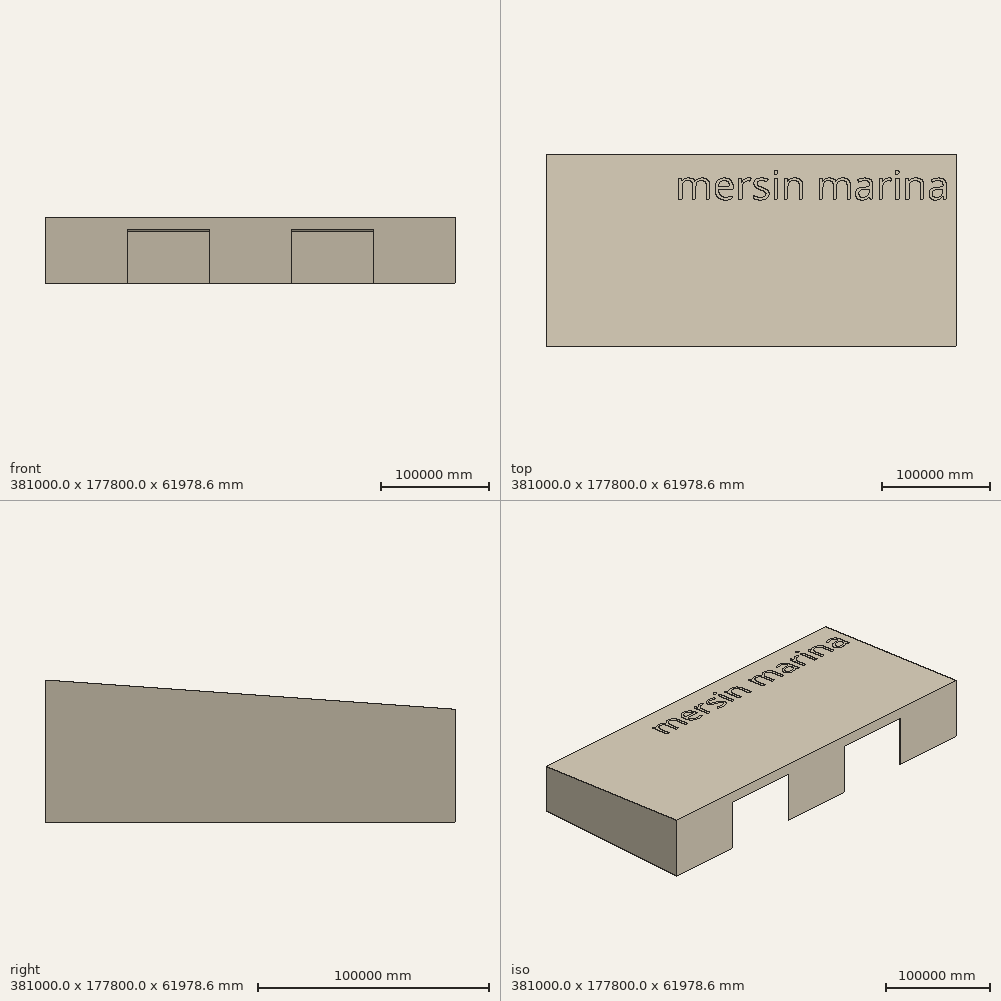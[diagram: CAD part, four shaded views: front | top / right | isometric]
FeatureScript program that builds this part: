
annotation { "Feature Type Name" : "Feature", "Feature Type Description" : "" }
export const myFeature = defineFeature(function(context is Context, id is Id, definition is map)
    precondition{}
    {
        {
            var Q0;
            Q0=qCreatedBy(makeId("Top.planeOp"),FACE);
            var sketch = newSketch(context, id + "F0", { "sketchPlane" : qUnion([Q0])});
            skLineSegment(sketch, "E0.bottom", {"start": v(0, 0) * mm, "end": v(381000, 0) * mm});
            skLineSegment(sketch, "E0.top", {"start": v(0, 177800) * mm, "end": v(381000, 177800) * mm});
            skLineSegment(sketch, "E0.left", {"start": v(0, 0) * mm, "end": v(0, 177800) * mm});
            skLineSegment(sketch, "E0.right", {"start": v(381000, 0) * mm, "end": v(381000, 177800) * mm});
            skLineSegment(sketch, "E1.0", {"start": v(1016, 176784) * mm, "end": v(379984, 176784) * mm});
            skLineSegment(sketch, "E1.1", {"start": v(1016, 1016) * mm, "end": v(1016, 176784) * mm});
            skLineSegment(sketch, "E1.2", {"start": v(1016, 1016) * mm, "end": v(379984, 1016) * mm});
            skLineSegment(sketch, "E1.3", {"start": v(379984, 1016) * mm, "end": v(379984, 176784) * mm});
            skSolve(sketch);
        }
        {
            var Q0;
            Q0 = qSketchRegion(id + "F0", true);
            extrude(context, id + "F1", {"entities" : qUnion([Q0]), "depth" : 60960 * mm, "offsetDistance" : 25.4 * mm});
        }
        {
            var Q0;
            Q0=makeQuery(id+"F1.opExtrude","SWEPT_FACE",FACE,{"disambiguationData":[OSD([sQuery(id+"F0.wireOp",EDGE,"E0.right")])]});
            var sketch = newSketch(context, id + "F2", { "sketchPlane" : qUnion([Q0])});
            skLineSegment(sketch, "E2", {"start": v(0, 60960) * mm, "end": v(177800, 48260) * mm});
            skLineSegment(sketch, "E3", {"start": v(177800, 48260) * mm, "end": v(177800, 60960) * mm});
            skLineSegment(sketch, "E4", {"start": v(177800, 60960) * mm, "end": v(0, 60960) * mm});
            skSolve(sketch);
        }
        {
            var Q0;
            Q0 = qSketchRegion(id + "F2", true);
            extrude(context, id + "F3", {"entities" : qUnion([Q0]), "operationType" : NewBodyOperationType.REMOVE, "oppositeDirection" : true, "depth" : 421894 * mm, "offsetDistance" : 25.4 * mm});
        }
        {
            var Q0;
            Q0=makeQuery(id+"F1.opExtrude","SWEPT_FACE",FACE,{"disambiguationData":[OSD([sQuery(id+"F0.wireOp",EDGE,"E0.right")])]});
            var sketch = newSketch(context, id + "F4", { "sketchPlane" : qUnion([Q0])});
            skLineSegment(sketch, "E5", {"start": v(177800, 48260) * mm, "end": v(0, 60960) * mm});
            skLineSegment(sketch, "E6.0", {"start": v(177800, 49278.59) * mm, "end": v(0, 61978.59) * mm});
            skLineSegment(sketch, "E7", {"start": v(0, 61978.59) * mm, "end": v(0, 60960) * mm});
            skLineSegment(sketch, "E8", {"start": v(177800, 48260) * mm, "end": v(177800, 49278.59) * mm});
            skSolve(sketch);
        }
        {
            var Q0;
            Q0 = qSketchRegion(id + "F4", true);
            extrude(context, id + "F5", {"entities" : qUnion([Q0]), "operationType" : NewBodyOperationType.ADD, "oppositeDirection" : true, "depth" : 381000 * mm, "offsetDistance" : 25.4 * mm});
        }
        {
            var Q0;
            Q0=makeQuery(id+"F1.opExtrude","SWEPT_FACE",FACE,{"disambiguationData":[OSD([sQuery(id+"F0.wireOp",EDGE,"E0.bottom")])]});
            var sketch = newSketch(context, id + "F6", { "sketchPlane" : qUnion([Q0])});
            skLineSegment(sketch, "E9.bottom", {"start": v(76200, 0) * mm, "end": v(152400, 0) * mm});
            skLineSegment(sketch, "E9.top", {"start": v(76200, 50800) * mm, "end": v(152400, 50800) * mm});
            skLineSegment(sketch, "E9.left", {"start": v(76200, 0) * mm, "end": v(76200, 50800) * mm});
            skLineSegment(sketch, "E9.right", {"start": v(152400, 0) * mm, "end": v(152400, 50800) * mm});
            skLineSegment(sketch, "E10.1.0.0", {"start": v(228600, 50800) * mm, "end": v(304800, 50800) * mm});
            skLineSegment(sketch, "E10.1.0.1", {"start": v(304800, 0) * mm, "end": v(304800, 50800) * mm});
            skLineSegment(sketch, "E10.1.0.2", {"start": v(228600, 0) * mm, "end": v(304800, 0) * mm});
            skLineSegment(sketch, "E10.1.0.3", {"start": v(228600, 0) * mm, "end": v(228600, 50800) * mm});
            skLineSegment(sketch, "E10.direction1", {"start": v(76200, 50800) * mm, "end": v(228600, 50800) * mm, "construction": true});
            skSolve(sketch);
        }
        {
            var Q0;
            Q0 = qSketchRegion(id + "F6", true);
            extrude(context, id + "F7", {"entities" : qUnion([Q0]), "operationType" : NewBodyOperationType.REMOVE, "oppositeDirection" : true, "depth" : 1270 * mm, "offsetDistance" : 25.4 * mm});
        }
        {
            var Q0;
            Q0=makeQuery(id+"F5.opExtrude","SWEPT_FACE",FACE,{"disambiguationData":[OSD([sQuery(id+"F4.wireOp",EDGE,"E6.0"),sQuery(id+"F4.wireOp",EDGE,"07e678e4-3284-47a3-8c32-3c2d062d193c.0")])]});
            var sketch = newSketch(context, id + "F8", { "sketchPlane" : qUnion([Q0])});
            skText(sketch, "E11", { "text": "mersin marina\n", "fontName": "OpenSans-Regular.ttf"});
            const initialGuessF8  = {"E11": [119.9001, 131.97287, 1, 0, 26.87683]};
            skSetInitialGuess(sketch, initialGuessF8);
            skSolve(sketch);
        }
        {
            var Q0;
            Q0 = qSketchRegion(id + "F8", true);
            extrude(context, id + "F9", {"entities" : qUnion([Q0]), "operationType" : NewBodyOperationType.ADD, "depth" : 25.4 * mm, "offsetDistance" : 25.4 * mm});
        }
    });
